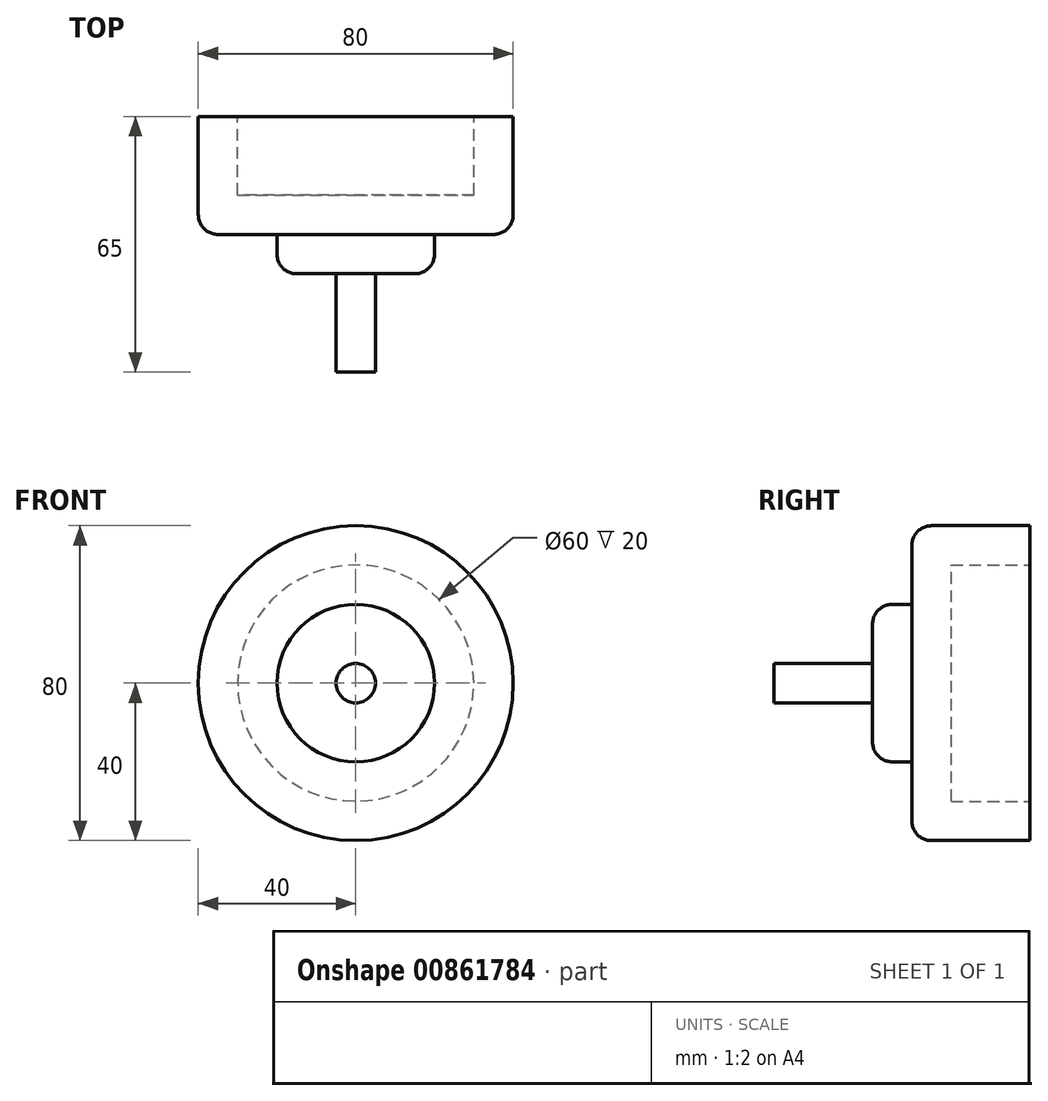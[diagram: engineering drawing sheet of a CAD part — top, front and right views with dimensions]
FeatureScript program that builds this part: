
annotation { "Feature Type Name" : "Feature", "Feature Type Description" : "" }
export const myFeature = defineFeature(function(context is Context, id is Id, definition is map)
    precondition{}
    {
        {
            var Q0;
            Q0=qCreatedBy(makeId("Front.planeOp"),FACE);
            var sketch = newSketch(context, id + "F0", { "sketchPlane" : qUnion([Q0])});
            skCircle(sketch, "E0", {"center": v(0, 0) * mm, "radius": 30 * mm});
            skCircle(sketch, "E1", {"center": v(0, 0) * mm, "radius": 40 * mm});
            skSolve(sketch);
        }
        {
            var Q0;
            Q0=makeQuery(id+"F0.imprint","IMPRINT",FACE,{"disambiguationData":[TD([[makeQuery(id+"F0.imprint","IMPRINT",EDGE,{"derivedFrom":sQuery(id+"F0.wireOp",EDGE,"E0")}),-1.0]])]});
            extrude(context, id + "F1", {"entities" : qUnion([Q0]), "depth" : 20 * mm, "offsetDistance" : 25 * mm});
        }
        {
            var Q0;
            Q0=makeQuery(id+"F1.opExtrude","CAP_FACE",FACE,{"disambiguationData":[OSD([sQuery(id+"F0.wireOp",EDGE,"E0"),sQuery(id+"F0.wireOp",EDGE,"E1")])],"isStart":false});
            var sketch = newSketch(context, id + "F2", { "sketchPlane" : qUnion([Q0])});
            skCircle(sketch, "E2", {"center": v(0, 0) * mm, "radius": 40 * mm});
            skSolve(sketch);
        }
        {
            var Q0;
            Q0=makeQuery(id+"F2.imprint","IMPRINT",FACE,{"disambiguationData":[TD([[makeQuery(id+"F2.imprint","IMPRINT",EDGE,{"derivedFrom":sQuery(id+"F2.wireOp",EDGE,"E2")}),1.0]])]});
            var Q1;
            Q1=makeQuery(id+"F2.imprint","IMPRINT",FACE,{"disambiguationData":[TD([[makeQuery(id+"F2.imprint","IMPRINT",EDGE,{"derivedFrom":makeQuery(id+"F1.opExtrude","CAP_EDGE",EDGE,{"disambiguationData":[OSD([sQuery(id+"F0.wireOp",EDGE,"E0")])],"isStart":false})}),1.0]])]});
            extrude(context, id + "F3", {"entities" : qUnion([Q0, Q1]), "operationType" : NewBodyOperationType.ADD, "depth" : 10 * mm, "offsetDistance" : 25 * mm});
        }
        {
            var Q0;
            Q0=makeQuery(id+"F3.opExtrude","CAP_FACE",FACE,{"disambiguationData":[OSD([sQuery(id+"F2.wireOp",EDGE,"E2")])],"isStart":false});
            var sketch = newSketch(context, id + "F4", { "sketchPlane" : qUnion([Q0])});
            skCircle(sketch, "E3", {"center": v(0, 0) * mm, "radius": 20 * mm});
            skSolve(sketch);
        }
        {
            var Q0;
            Q0=makeQuery(id+"F4.imprint","IMPRINT",FACE,{"disambiguationData":[TD([[makeQuery(id+"F4.imprint","IMPRINT",EDGE,{"derivedFrom":sQuery(id+"F4.wireOp",EDGE,"E3")}),1.0]])]});
            extrude(context, id + "F5", {"entities" : qUnion([Q0]), "operationType" : NewBodyOperationType.ADD, "depth" : 10 * mm, "offsetDistance" : 25 * mm});
        }
        {
            var Q0;
            Q0=makeQuery(id+"F5.opExtrude","CAP_FACE",FACE,{"disambiguationData":[OSD([sQuery(id+"F4.wireOp",EDGE,"E3")])],"isStart":false});
            var sketch = newSketch(context, id + "F6", { "sketchPlane" : qUnion([Q0])});
            skCircle(sketch, "E4", {"center": v(0, 0) * mm, "radius": 5 * mm});
            skSolve(sketch);
        }
        {
            var Q0;
            Q0=makeQuery(id+"F6.imprint","IMPRINT",FACE,{"disambiguationData":[TD([[makeQuery(id+"F6.imprint","IMPRINT",EDGE,{"derivedFrom":sQuery(id+"F6.wireOp",EDGE,"E4")}),1.0]])]});
            extrude(context, id + "F7", {"entities" : qUnion([Q0]), "operationType" : NewBodyOperationType.ADD, "depth" : 25 * mm, "offsetDistance" : 25 * mm});
        }
        {
            var Q0;
            Q0=makeQuery(id+"F5.opExtrude","CAP_EDGE",EDGE,{"disambiguationData":[OSD([sQuery(id+"F4.wireOp",EDGE,"E3")])],"isStart":true});
            var Q1;
            Q1=makeQuery(id+"F5.opExtrude","CAP_EDGE",EDGE,{"disambiguationData":[OSD([sQuery(id+"F4.wireOp",EDGE,"E3")])],"isStart":false});
            fillet(context, id + "F8", {"entities" : qUnion([Q0, Q1]), "radius" : 5 * mm, "tangentPropagation" : true, "allowEdgeOverflow" : false});
        }
        {
            var Q0;
            Q0=makeQuery(id+"F3.opExtrude","CAP_EDGE",EDGE,{"disambiguationData":[OSD([sQuery(id+"F2.wireOp",EDGE,"E2")])],"isStart":false});
            fillet(context, id + "F9", {"entities" : qUnion([Q0]), "radius" : 5 * mm, "tangentPropagation" : true, "allowEdgeOverflow" : false});
        }
    });
